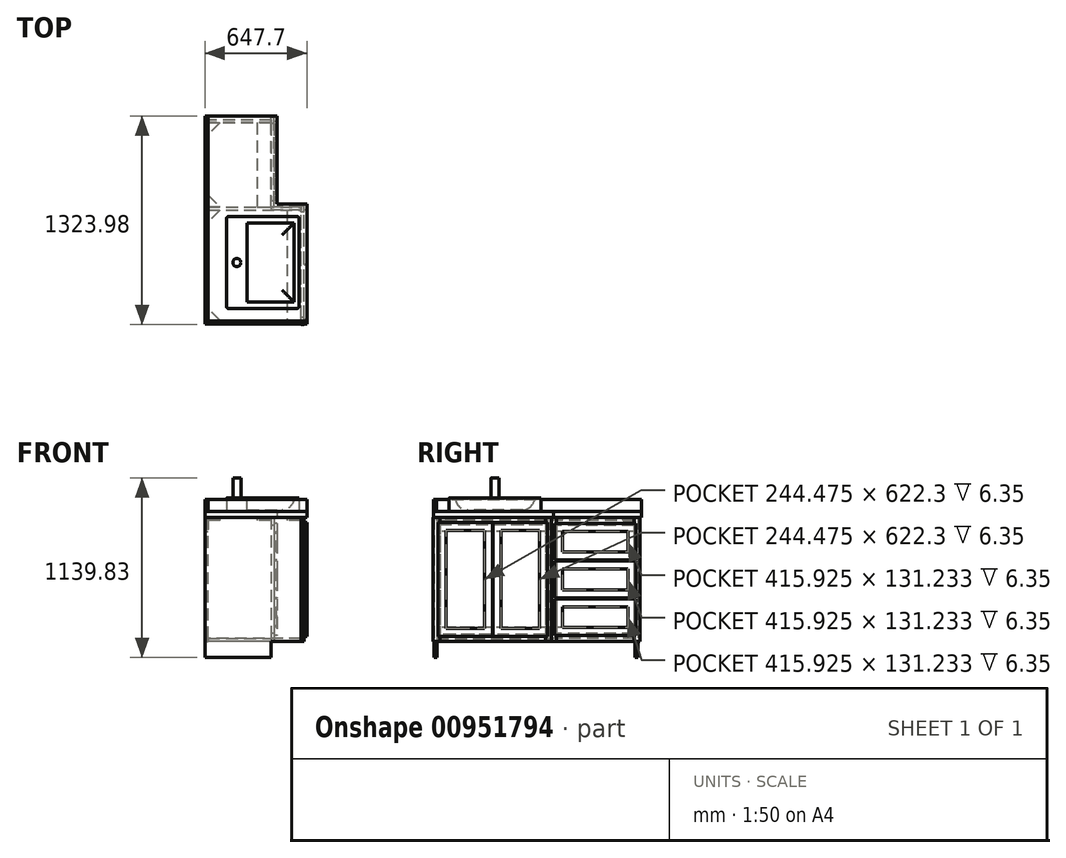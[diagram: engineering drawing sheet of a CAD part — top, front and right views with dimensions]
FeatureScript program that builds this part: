
annotation { "Feature Type Name" : "Feature", "Feature Type Description" : "" }
export const myFeature = defineFeature(function(context is Context, id is Id, definition is map)
    precondition{}
    {
        {
            var Q0;
            Q0=qCreatedBy(makeId("Top.planeOp"),FACE);
            var sketch = newSketch(context, id + "F0", { "sketchPlane" : qUnion([Q0])});
            skLineSegment(sketch, "E0", {"start": v(-384.18, 0) * mm, "end": v(384.18, 0) * mm});
            skLineSegment(sketch, "E1", {"start": v(-384.18, 0) * mm, "end": v(-1247.78, 0) * mm});
            skLineSegment(sketch, "E2", {"start": v(-1247.78, 0) * mm, "end": v(-1247.78, 2298.7) * mm});
            skLineSegment(sketch, "E3", {"start": v(-1247.78, 2298.7) * mm, "end": v(206.37, 2298.7) * mm});
            skLineSegment(sketch, "E4", {"start": v(206.37, 2298.7) * mm, "end": v(206.37, 1555.75) * mm});
            skLineSegment(sketch, "E5", {"start": v(206.37, 1555.75) * mm, "end": v(574.68, 1555.75) * mm});
            skLineSegment(sketch, "E6", {"start": v(574.68, 1555.75) * mm, "end": v(574.68, 0) * mm});
            skLineSegment(sketch, "E7", {"start": v(574.68, 0) * mm, "end": v(384.18, 0) * mm});
            skLineSegment(sketch, "E8", {"start": v(206.37, 1555.75) * mm, "end": v(-1247.78, 1555.75) * mm, "construction": true});
            skLineSegment(sketch, "E9", {"start": v(219.08, 1327.15) * mm, "end": v(219.08, 819.15) * mm, "construction": true});
            skLineSegment(sketch, "E10", {"start": v(-136.53, 1073.15) * mm, "end": v(574.68, 1073.15) * mm, "construction": true});
            skPoint(sketch, "E11", {"position": v(219.08, 1073.15) * mm});
            skLineSegment(sketch, "E12", {"start": v(-1247.78, 1320.8) * mm, "end": v(-790.58, 1320.8) * mm, "construction": true});
            skLineSegment(sketch, "E13", {"start": v(-790.57, 1320.8) * mm, "end": v(-790.57, 762) * mm, "construction": true});
            skLineSegment(sketch, "E14", {"start": v(-790.58, 762) * mm, "end": v(-600.07, 762) * mm, "construction": true});
            skLineSegment(sketch, "E15", {"start": v(-600.07, 762) * mm, "end": v(-600.07, 0) * mm, "construction": true});
            skEllipse(sketch, "E16", {"center": v(219.08, 1073.15) * mm, "majorRadius": 355.6 * mm, "minorRadius": 254 * mm, "majorAxis": v(1, 0)});
            skLineSegment(sketch, "E17", {"start": v(-1228.73, 1320.8) * mm, "end": v(-1228.72, 0) * mm, "construction": true});
            skLineSegment(sketch, "E18", {"start": v(-1228.72, 19.05) * mm, "end": v(-600.07, 19.05) * mm, "construction": true});
            skLineSegment(sketch, "E19.bottom", {"start": v(-650.87, 98.43) * mm, "end": v(-1111.25, 98.43) * mm});
            skLineSegment(sketch, "E19.top", {"start": v(-650.87, 682.63) * mm, "end": v(-1111.25, 682.63) * mm});
            skLineSegment(sketch, "E19.left", {"start": v(-650.87, 98.43) * mm, "end": v(-650.87, 682.63) * mm});
            skLineSegment(sketch, "E19.right", {"start": v(-1111.25, 98.43) * mm, "end": v(-1111.25, 682.63) * mm});
            skPoint(sketch, "E19.middle", {"position": v(-881.06, 390.53) * mm});
            skLineSegment(sketch, "E20", {"start": v(-1111.25, 390.53) * mm, "end": v(-1228.73, 390.53) * mm, "construction": true});
            skLineSegment(sketch, "E21", {"start": v(-881.06, 98.43) * mm, "end": v(-881.06, 19.05) * mm, "construction": true});
            skLineSegment(sketch, "E22", {"start": v(-650.87, 390.53) * mm, "end": v(-600.07, 390.53) * mm, "construction": true});
            skLineSegment(sketch, "E23", {"start": v(-650.87, 682.63) * mm, "end": v(-650.87, 762) * mm, "construction": true});
            skSolve(sketch);
        }
        {
            var Q0;
            Q0=qCreatedBy(makeId("Top.planeOp"),FACE);
            var sketch = newSketch(context, id + "F1", { "sketchPlane" : qUnion([Q0])});
            skLineSegment(sketch, "E24.bottom", {"start": v(-1247.78, 3.17) * mm, "end": v(-638.17, 3.17) * mm});
            skLineSegment(sketch, "E24.top", {"start": v(-1247.78, 22.23) * mm, "end": v(-638.17, 22.23) * mm});
            skLineSegment(sketch, "E24.left", {"start": v(-1247.78, 3.17) * mm, "end": v(-1247.78, 22.22) * mm});
            skLineSegment(sketch, "E24.right", {"start": v(-638.17, 3.17) * mm, "end": v(-638.17, 22.23) * mm});
            skLineSegment(sketch, "E25.bottom", {"start": v(-1247.78, 742.95) * mm, "end": v(-638.18, 742.95) * mm});
            skLineSegment(sketch, "E25.top", {"start": v(-1247.78, 723.9) * mm, "end": v(-638.18, 723.9) * mm});
            skLineSegment(sketch, "E25.left", {"start": v(-1247.78, 742.95) * mm, "end": v(-1247.78, 723.9) * mm});
            skLineSegment(sketch, "E25.right", {"start": v(-638.18, 742.95) * mm, "end": v(-638.18, 723.9) * mm});
            skLineSegment(sketch, "E26.bottom", {"start": v(-1247.78, 1298.58) * mm, "end": v(-828.67, 1298.58) * mm});
            skLineSegment(sketch, "E26.top", {"start": v(-1247.78, 1279.53) * mm, "end": v(-828.67, 1279.53) * mm});
            skLineSegment(sketch, "E26.left", {"start": v(-1247.78, 1298.58) * mm, "end": v(-1247.78, 1279.53) * mm});
            skLineSegment(sketch, "E26.right", {"start": v(-828.67, 1298.58) * mm, "end": v(-828.67, 1279.53) * mm});
            skLineSegment(sketch, "E27.bottom", {"start": v(-619.12, 0) * mm, "end": v(-638.17, 0) * mm, "construction": true});
            skLineSegment(sketch, "E27.top", {"start": v(-619.12, 50.8) * mm, "end": v(-638.17, 50.8) * mm, "construction": true});
            skLineSegment(sketch, "E27.left", {"start": v(-619.12, 0) * mm, "end": v(-619.12, 50.8) * mm, "construction": true});
            skLineSegment(sketch, "E27.right", {"start": v(-638.17, 0) * mm, "end": v(-638.17, 50.8) * mm, "construction": true});
            skLineSegment(sketch, "E28.bottom", {"start": v(-619.12, 692.15) * mm, "end": v(-638.18, 692.15) * mm, "construction": true});
            skLineSegment(sketch, "E28.top", {"start": v(-619.12, 742.95) * mm, "end": v(-638.18, 742.95) * mm, "construction": true});
            skLineSegment(sketch, "E28.left", {"start": v(-619.12, 692.15) * mm, "end": v(-619.12, 742.95) * mm, "construction": true});
            skLineSegment(sketch, "E28.right", {"start": v(-638.18, 692.15) * mm, "end": v(-638.18, 742.95) * mm, "construction": true});
            skLineSegment(sketch, "E29.bottom", {"start": v(-809.62, 1301.75) * mm, "end": v(-828.67, 1301.75) * mm, "construction": true});
            skLineSegment(sketch, "E29.top", {"start": v(-809.62, 1250.95) * mm, "end": v(-828.67, 1250.95) * mm, "construction": true});
            skLineSegment(sketch, "E29.left", {"start": v(-809.62, 1301.75) * mm, "end": v(-809.62, 1250.95) * mm, "construction": true});
            skLineSegment(sketch, "E29.right", {"start": v(-828.67, 1301.75) * mm, "end": v(-828.67, 1250.95) * mm, "construction": true});
            skLineSegment(sketch, "E30", {"start": v(-828.67, 1250.95) * mm, "end": v(-828.67, 793.75) * mm, "construction": true});
            skLineSegment(sketch, "E31", {"start": v(-809.62, 1250.95) * mm, "end": v(-809.62, 793.75) * mm, "construction": true});
            skLineSegment(sketch, "E32", {"start": v(-638.18, 692.15) * mm, "end": v(-638.17, 50.8) * mm, "construction": true});
            skLineSegment(sketch, "E33", {"start": v(-619.12, 50.8) * mm, "end": v(-619.12, 692.15) * mm, "construction": true});
            skLineSegment(sketch, "E34.bottom", {"start": v(-828.67, 793.75) * mm, "end": v(-809.62, 793.75) * mm, "construction": true});
            skLineSegment(sketch, "E34.top", {"start": v(-828.67, 742.95) * mm, "end": v(-809.62, 742.95) * mm, "construction": true});
            skLineSegment(sketch, "E34.left", {"start": v(-828.67, 793.75) * mm, "end": v(-828.67, 742.95) * mm, "construction": true});
            skLineSegment(sketch, "E34.right", {"start": v(-809.62, 793.75) * mm, "end": v(-809.62, 742.95) * mm, "construction": true});
            skSolve(sketch);
        }
        {
            var Q0;
            Q0 = qSketchRegion(id + "F1", true);
            extrude(context, id + "F2", {"entities" : qUnion([Q0]), "depth" : 889 * mm, "offsetDistance" : 25.4 * mm});
        }
        {
            var Q0;
            Q0=makeQuery(id+"F2.opExtrude","SWEPT_FACE",FACE,{"disambiguationData":[OSD([sQuery(id+"F1.wireOp",EDGE,"E24.bottom")])]});
            var sketch = newSketch(context, id + "F3", { "sketchPlane" : qUnion([Q0])});
            skLineSegment(sketch, "E35.bottom", {"start": v(-1247.78, 0) * mm, "end": v(-638.17, 0) * mm, "construction": true});
            skLineSegment(sketch, "E35.top", {"start": v(-1247.78, 101.6) * mm, "end": v(-638.17, 101.6) * mm, "construction": true});
            skLineSegment(sketch, "E35.left", {"start": v(-1247.78, 0) * mm, "end": v(-1247.78, 101.6) * mm, "construction": true});
            skLineSegment(sketch, "E35.right", {"start": v(-638.17, 0) * mm, "end": v(-638.17, 101.6) * mm});
            skLineSegment(sketch, "E36", {"start": v(-828.67, 101.6) * mm, "end": v(-828.67, 0) * mm});
            skLineSegment(sketch, "E37", {"start": v(-828.67, 101.6) * mm, "end": v(-638.17, 101.6) * mm});
            skLineSegment(sketch, "E38", {"start": v(-828.67, 0) * mm, "end": v(-638.17, 0) * mm});
            skSolve(sketch);
        }
        {
            var Q0;
            Q0 = qSketchRegion(id + "F3", true);
            extrude(context, id + "F4", {"entities" : qUnion([Q0]), "operationType" : NewBodyOperationType.REMOVE, "endBound" : BoundingType.THROUGH_ALL, "oppositeDirection" : true, "depth" : 25.4 * mm, "offsetDistance" : 25.4 * mm});
        }
        {
            var Q0;
            Q0=makeQuery(id+"F2.opExtrude","SWEPT_FACE",FACE,{"disambiguationData":[OSD([sQuery(id+"F1.wireOp",EDGE,"E24.right")])]});
            var sketch = newSketch(context, id + "F5", { "sketchPlane" : qUnion([Q0])});
            skLineSegment(sketch, "E39.bottom", {"start": v(-3.17, 889) * mm, "end": v(41.28, 889) * mm});
            skLineSegment(sketch, "E39.top", {"start": v(-3.17, 101.6) * mm, "end": v(41.28, 101.6) * mm});
            skLineSegment(sketch, "E39.left", {"start": v(-3.17, 889) * mm, "end": v(-3.17, 101.6) * mm});
            skLineSegment(sketch, "E39.right", {"start": v(41.28, 889) * mm, "end": v(41.28, 101.6) * mm});
            skLineSegment(sketch, "E40.bottom", {"start": v(711.2, 889) * mm, "end": v(749.3, 889) * mm});
            skLineSegment(sketch, "E40.top", {"start": v(711.2, 101.6) * mm, "end": v(749.3, 101.6) * mm});
            skLineSegment(sketch, "E40.left", {"start": v(711.2, 889) * mm, "end": v(711.2, 101.6) * mm});
            skLineSegment(sketch, "E40.right", {"start": v(749.3, 889) * mm, "end": v(749.3, 101.6) * mm});
            skSolve(sketch);
        }
        {
            var Q0;
            Q0 = qSketchRegion(id + "F5", true);
            extrude(context, id + "F6", {"entities" : qUnion([Q0]), "depth" : 19.05 * mm, "offsetDistance" : 25.4 * mm});
        }
        {
            var Q0;
            Q0=makeQuery(id+"F2.opExtrude","SWEPT_FACE",FACE,{"disambiguationData":[OSD([sQuery(id+"F1.wireOp",EDGE,"E26.right")])]});
            var sketch = newSketch(context, id + "F7", { "sketchPlane" : qUnion([Q0])});
            skLineSegment(sketch, "E41.bottom", {"start": v(1273.17, 889) * mm, "end": v(1311.27, 889) * mm});
            skLineSegment(sketch, "E41.top", {"start": v(1273.18, 101.6) * mm, "end": v(1311.27, 101.6) * mm});
            skLineSegment(sketch, "E41.left", {"start": v(1273.17, 889) * mm, "end": v(1273.17, 101.6) * mm});
            skLineSegment(sketch, "E41.right", {"start": v(1311.27, 889) * mm, "end": v(1311.27, 101.6) * mm});
            skLineSegment(sketch, "E42.bottom", {"start": v(742.95, 889) * mm, "end": v(781.05, 889) * mm});
            skLineSegment(sketch, "E42.top", {"start": v(742.95, 101.6) * mm, "end": v(781.05, 101.6) * mm});
            skLineSegment(sketch, "E42.left", {"start": v(742.95, 889) * mm, "end": v(742.95, 101.6) * mm});
            skLineSegment(sketch, "E42.right", {"start": v(781.05, 889) * mm, "end": v(781.05, 101.6) * mm});
            skSolve(sketch);
        }
        {
            var Q0;
            Q0 = qSketchRegion(id + "F7", true);
            extrude(context, id + "F8", {"entities" : qUnion([Q0]), "depth" : 19.05 * mm, "offsetDistance" : 25.4 * mm});
        }
        {
            var Q0;
            Q0=makeQuery(id+"F4.boolean.opBoolean","COPY",FACE,{"disambiguationData":[TD([makeQuery(id+"F2.opExtrude","SWEPT_FACE",FACE,{"disambiguationData":[OSD([sQuery(id+"F1.wireOp",EDGE,"E24.bottom")])]})])],"derivedFrom":makeQuery(id+"F4.opExtrude","SWEPT_FACE",FACE,{"disambiguationData":[OSD([sQuery(id+"F3.wireOp",EDGE,"E37")])]})});
            var sketch = newSketch(context, id + "F9", { "sketchPlane" : qUnion([Q0])});
            skLineSegment(sketch, "E43", {"start": v(-638.18, -22.22) * mm, "end": v(-1228.73, -22.23) * mm});
            skLineSegment(sketch, "E44", {"start": v(-638.18, -22.23) * mm, "end": v(-638.18, -723.9) * mm});
            skLineSegment(sketch, "E45", {"start": v(-828.67, -723.9) * mm, "end": v(-638.17, -723.9) * mm});
            skLineSegment(sketch, "E46", {"start": v(-828.67, -723.9) * mm, "end": v(-828.67, -1279.53) * mm});
            skLineSegment(sketch, "E47", {"start": v(-828.67, -1279.53) * mm, "end": v(-1228.73, -1279.53) * mm});
            skLineSegment(sketch, "E48", {"start": v(-1228.73, -1279.53) * mm, "end": v(-1228.73, -22.23) * mm});
            skSolve(sketch);
        }
        {
            var Q0;
            Q0 = qSketchRegion(id + "F9", true);
            extrude(context, id + "F10", {"entities" : qUnion([Q0]), "oppositeDirection" : true, "depth" : 19.05 * mm, "offsetDistance" : 25.4 * mm});
        }
        {
            var Q0;
            Q0=makeQuery(id+"F2.opExtrude","CAP_FACE",FACE,{"disambiguationData":[OSD([sQuery(id+"F1.wireOp",EDGE,"E25.bottom"),sQuery(id+"F1.wireOp",EDGE,"E25.top"),sQuery(id+"F1.wireOp",EDGE,"E25.left"),sQuery(id+"F1.wireOp",EDGE,"E25.right")])],"isStart":true});
            var sketch = newSketch(context, id + "F11", { "sketchPlane" : qUnion([Q0])});
            skLineSegment(sketch, "E49.0", {"start": v(-1247.78, -742.95) * mm, "end": v(-828.68, -742.95) * mm});
            skLineSegment(sketch, "E50.0", {"start": v(-828.67, -742.95) * mm, "end": v(-828.67, -723.9) * mm});
            skLineSegment(sketch, "E51.0", {"start": v(-1247.78, -723.9) * mm, "end": v(-828.67, -723.9) * mm});
            skLineSegment(sketch, "E52.0", {"start": v(-1247.78, -742.95) * mm, "end": v(-1247.78, -723.9) * mm});
            skSolve(sketch);
        }
        {
            var Q0;
            Q0 = qSketchRegion(id + "F11", true);
            extrude(context, id + "F12", {"entities" : qUnion([Q0]), "operationType" : NewBodyOperationType.REMOVE, "oppositeDirection" : true, "depth" : 120.65 * mm, "offsetDistance" : 25.4 * mm});
        }
        {
            var Q0;
            Q0=makeQuery(id+"F2.opExtrude","SWEPT_FACE",FACE,{"disambiguationData":[OSD([sQuery(id+"F1.wireOp",EDGE,"E25.bottom")])]});
            var sketch = newSketch(context, id + "F13", { "sketchPlane" : qUnion([Q0])});
            skLineSegment(sketch, "E53.bottom", {"start": v(1247.78, 120.65) * mm, "end": v(1228.73, 120.65) * mm});
            skLineSegment(sketch, "E53.top", {"start": v(1247.78, 889) * mm, "end": v(1228.73, 889) * mm});
            skLineSegment(sketch, "E53.left", {"start": v(1247.78, 120.65) * mm, "end": v(1247.78, 889) * mm});
            skLineSegment(sketch, "E53.right", {"start": v(1228.73, 120.65) * mm, "end": v(1228.73, 889) * mm});
            skSolve(sketch);
        }
        {
            var Q0;
            Q0 = qSketchRegion(id + "F13", true);
            extrude(context, id + "F14", {"entities" : qUnion([Q0]), "operationType" : NewBodyOperationType.REMOVE, "endBound" : BoundingType.UP_TO_NEXT, "oppositeDirection" : true, "depth" : 25.4 * mm, "offsetDistance" : 25.4 * mm});
        }
        {
            var Q0;
            Q0=makeQuery(id+"F6.opExtrude","CAP_FACE",FACE,{"disambiguationData":[OSD([sQuery(id+"F5.wireOp",EDGE,"E39.bottom"),sQuery(id+"F5.wireOp",EDGE,"E39.top"),sQuery(id+"F5.wireOp",EDGE,"E39.left"),sQuery(id+"F5.wireOp",EDGE,"E39.right")])],"isStart":false});
            var sketch = newSketch(context, id + "F15", { "sketchPlane" : qUnion([Q0])});
            skLineSegment(sketch, "E54.bottom", {"start": v(41.28, 889) * mm, "end": v(711.2, 889) * mm});
            skLineSegment(sketch, "E54.top", {"start": v(41.28, 844.55) * mm, "end": v(711.2, 844.55) * mm});
            skLineSegment(sketch, "E54.left", {"start": v(41.28, 889) * mm, "end": v(41.28, 844.55) * mm});
            skLineSegment(sketch, "E54.right", {"start": v(711.2, 889) * mm, "end": v(711.2, 844.55) * mm});
            skLineSegment(sketch, "E55.bottom", {"start": v(711.2, 101.6) * mm, "end": v(41.28, 101.6) * mm});
            skLineSegment(sketch, "E55.top", {"start": v(711.2, 146.05) * mm, "end": v(41.28, 146.05) * mm});
            skLineSegment(sketch, "E55.left", {"start": v(711.2, 101.6) * mm, "end": v(711.2, 146.05) * mm});
            skLineSegment(sketch, "E55.right", {"start": v(41.28, 101.6) * mm, "end": v(41.28, 146.05) * mm});
            skSolve(sketch);
        }
        {
            var Q0;
            Q0 = qSketchRegion(id + "F15", true);
            extrude(context, id + "F16", {"entities" : qUnion([Q0]), "oppositeDirection" : true, "depth" : 19.05 * mm, "offsetDistance" : 25.4 * mm});
        }
        {
            var Q0;
            Q0=makeQuery(id+"F8.opExtrude","SWEPT_FACE",FACE,{"disambiguationData":[OSD([sQuery(id+"F7.wireOp",EDGE,"E42.right")])]});
            var sketch = newSketch(context, id + "F17", { "sketchPlane" : qUnion([Q0])});
            skLineSegment(sketch, "E56.bottom", {"start": v(809.62, 889) * mm, "end": v(828.67, 889) * mm});
            skLineSegment(sketch, "E56.top", {"start": v(809.62, 838.2) * mm, "end": v(828.67, 838.2) * mm});
            skLineSegment(sketch, "E56.left", {"start": v(809.62, 889) * mm, "end": v(809.62, 838.2) * mm});
            skLineSegment(sketch, "E56.right", {"start": v(828.67, 889) * mm, "end": v(828.67, 838.2) * mm});
            skLineSegment(sketch, "E57.bottom", {"start": v(809.62, 101.6) * mm, "end": v(828.67, 101.6) * mm});
            skLineSegment(sketch, "E57.top", {"start": v(809.62, 152.4) * mm, "end": v(828.67, 152.4) * mm});
            skLineSegment(sketch, "E57.left", {"start": v(809.62, 101.6) * mm, "end": v(809.62, 152.4) * mm});
            skLineSegment(sketch, "E57.right", {"start": v(828.67, 101.6) * mm, "end": v(828.67, 152.4) * mm});
            skSolve(sketch);
        }
        {
            var Q0;
            Q0 = qSketchRegion(id + "F17", true);
            var Q1;
            Q1=makeQuery(id+"F8.opExtrude","SWEPT_FACE",FACE,{"disambiguationData":[OSD([sQuery(id+"F7.wireOp",EDGE,"E41.left")])]});
            extrude(context, id + "F18", {"entities" : qUnion([Q0]), "endBound" : BoundingType.UP_TO_SURFACE, "depth" : 25.4 * mm, "endBoundEntityFace" : qUnion([Q1]), "offsetDistance" : 25.4 * mm});
        }
        {
            var Q0;
            Q0=makeQuery(id+"F2.opExtrude","SWEPT_FACE",FACE,{"disambiguationData":[OSD([sQuery(id+"F1.wireOp",EDGE,"E24.top")])]});
            var sketch = newSketch(context, id + "F19", { "sketchPlane" : qUnion([Q0])});
            skLineSegment(sketch, "E58.bottom", {"start": v(1247.78, 889) * mm, "end": v(1228.72, 889) * mm});
            skLineSegment(sketch, "E58.top", {"start": v(1247.78, 800.1) * mm, "end": v(1228.72, 800.1) * mm});
            skLineSegment(sketch, "E58.left", {"start": v(1247.78, 889) * mm, "end": v(1247.78, 800.1) * mm});
            skLineSegment(sketch, "E58.right", {"start": v(1228.72, 889) * mm, "end": v(1228.72, 800.1) * mm});
            skLineSegment(sketch, "E59.bottom", {"start": v(1247.78, 101.6) * mm, "end": v(1228.73, 101.6) * mm});
            skLineSegment(sketch, "E59.top", {"start": v(1247.78, 190.5) * mm, "end": v(1228.73, 190.5) * mm});
            skLineSegment(sketch, "E59.left", {"start": v(1247.78, 101.6) * mm, "end": v(1247.78, 190.5) * mm});
            skLineSegment(sketch, "E59.right", {"start": v(1228.73, 101.6) * mm, "end": v(1228.73, 190.5) * mm});
            skSolve(sketch);
        }
        {
            var Q0;
            Q0 = qSketchRegion(id + "F19", true);
            var Q1;
            Q1=makeQuery(id+"F2.opExtrude","SWEPT_FACE",FACE,{"disambiguationData":[OSD([sQuery(id+"F1.wireOp",EDGE,"E26.top")])]});
            extrude(context, id + "F20", {"entities" : qUnion([Q0]), "endBound" : BoundingType.UP_TO_SURFACE, "depth" : 25.4 * mm, "endBoundEntityFace" : qUnion([Q1]), "offsetDistance" : 25.4 * mm});
        }
        {
            var Q0;
            Q0=makeQuery(id+"F2.opExtrude","SWEPT_FACE",FACE,{"disambiguationData":[OSD([sQuery(id+"F1.wireOp",EDGE,"E24.top")])]});
            var sketch = newSketch(context, id + "F21", { "sketchPlane" : qUnion([Q0])});
            skLineSegment(sketch, "E60.bottom", {"start": v(638.17, 889) * mm, "end": v(727.07, 889) * mm});
            skLineSegment(sketch, "E60.top", {"start": v(638.17, 869.95) * mm, "end": v(727.07, 869.95) * mm});
            skLineSegment(sketch, "E60.left", {"start": v(638.17, 889) * mm, "end": v(638.17, 869.95) * mm});
            skLineSegment(sketch, "E60.right", {"start": v(727.07, 889) * mm, "end": v(727.07, 869.95) * mm});
            skSolve(sketch);
        }
        {
            var Q0;
            Q0 = qSketchRegion(id + "F21", true);
            var Q1;
            Q1=makeQuery(id+"F2.opExtrude","SWEPT_FACE",FACE,{"disambiguationData":[OSD([sQuery(id+"F1.wireOp",EDGE,"E25.top")])]});
            extrude(context, id + "F22", {"entities" : qUnion([Q0]), "endBound" : BoundingType.UP_TO_SURFACE, "depth" : 25.4 * mm, "endBoundEntityFace" : qUnion([Q1]), "offsetDistance" : 25.4 * mm});
        }
        {
            var Q0;
            Q0=makeQuery(id+"F2.opExtrude","SWEPT_FACE",FACE,{"disambiguationData":[OSD([sQuery(id+"F1.wireOp",EDGE,"E25.bottom")])]});
            var sketch = newSketch(context, id + "F23", { "sketchPlane" : qUnion([Q0])});
            skLineSegment(sketch, "E61.bottom", {"start": v(828.67, 889) * mm, "end": v(917.57, 889) * mm});
            skLineSegment(sketch, "E61.top", {"start": v(828.67, 869.95) * mm, "end": v(917.57, 869.95) * mm});
            skLineSegment(sketch, "E61.left", {"start": v(828.67, 889) * mm, "end": v(828.67, 869.95) * mm});
            skLineSegment(sketch, "E61.right", {"start": v(917.57, 889) * mm, "end": v(917.57, 869.95) * mm});
            skSolve(sketch);
        }
        {
            var Q0;
            Q0 = qSketchRegion(id + "F23", true);
            var Q1;
            Q1=makeQuery(id+"F2.opExtrude","SWEPT_FACE",FACE,{"disambiguationData":[OSD([sQuery(id+"F1.wireOp",EDGE,"E26.top")])]});
            extrude(context, id + "F24", {"entities" : qUnion([Q0]), "endBound" : BoundingType.UP_TO_SURFACE, "depth" : 25.4 * mm, "endBoundEntityFace" : qUnion([Q1]), "offsetDistance" : 25.4 * mm});
        }
        {
            var Q0;
            Q0=makeQuery(id+"F2.opExtrude","CAP_FACE",FACE,{"disambiguationData":[OSD([sQuery(id+"F1.wireOp",EDGE,"E24.bottom"),sQuery(id+"F1.wireOp",EDGE,"E24.top"),sQuery(id+"F1.wireOp",EDGE,"E24.left"),sQuery(id+"F1.wireOp",EDGE,"E24.right")])],"isStart":false});
            var sketch = newSketch(context, id + "F25", { "sketchPlane" : qUnion([Q0])});
            skLineSegment(sketch, "E62", {"start": v(-1152.52, 22.23) * mm, "end": v(-1228.72, 98.43) * mm});
            skLineSegment(sketch, "E63", {"start": v(-1228.72, 98.43) * mm, "end": v(-1228.72, 22.23) * mm});
            skLineSegment(sketch, "E64", {"start": v(-1228.72, 22.23) * mm, "end": v(-1152.52, 22.23) * mm});
            skLineSegment(sketch, "E65", {"start": v(-1228.72, 647.7) * mm, "end": v(-1228.72, 723.9) * mm});
            skLineSegment(sketch, "E66", {"start": v(-1228.73, 723.9) * mm, "end": v(-1152.53, 723.9) * mm});
            skLineSegment(sketch, "E67", {"start": v(-1152.53, 723.9) * mm, "end": v(-1228.73, 647.7) * mm});
            skLineSegment(sketch, "E68", {"start": v(-1152.53, 742.95) * mm, "end": v(-1228.73, 742.95) * mm});
            skLineSegment(sketch, "E69", {"start": v(-1228.73, 742.95) * mm, "end": v(-1228.73, 819.15) * mm});
            skLineSegment(sketch, "E70", {"start": v(-1228.72, 819.15) * mm, "end": v(-1152.52, 742.95) * mm});
            skLineSegment(sketch, "E71", {"start": v(-1228.72, 1203.33) * mm, "end": v(-1228.72, 1279.53) * mm});
            skLineSegment(sketch, "E72", {"start": v(-1228.72, 1279.53) * mm, "end": v(-1152.52, 1279.53) * mm});
            skLineSegment(sketch, "E73", {"start": v(-1152.52, 1279.53) * mm, "end": v(-1228.72, 1203.33) * mm});
            skSolve(sketch);
        }
        {
            var Q0;
            Q0 = qSketchRegion(id + "F25", true);
            extrude(context, id + "F26", {"entities" : qUnion([Q0]), "oppositeDirection" : true, "depth" : 19.05 * mm, "offsetDistance" : 25.4 * mm});
        }
        {
            var Q0;
            Q0=makeQuery(id+"F6.opExtrude","CAP_FACE",FACE,{"disambiguationData":[OSD([sQuery(id+"F5.wireOp",EDGE,"E39.bottom"),sQuery(id+"F5.wireOp",EDGE,"E39.top"),sQuery(id+"F5.wireOp",EDGE,"E39.left"),sQuery(id+"F5.wireOp",EDGE,"E39.right")])],"isStart":false});
            var sketch = newSketch(context, id + "F27", { "sketchPlane" : qUnion([Q0])});
            skLineSegment(sketch, "E74.bottom", {"start": v(28.58, 857.25) * mm, "end": v(374.65, 857.25) * mm});
            skLineSegment(sketch, "E74.top", {"start": v(28.58, 133.35) * mm, "end": v(374.65, 133.35) * mm});
            skLineSegment(sketch, "E74.left", {"start": v(28.58, 857.25) * mm, "end": v(28.58, 133.35) * mm});
            skLineSegment(sketch, "E74.right", {"start": v(374.65, 857.25) * mm, "end": v(374.65, 133.35) * mm});
            skLineSegment(sketch, "E75.bottom", {"start": v(377.83, 133.35) * mm, "end": v(723.9, 133.35) * mm});
            skLineSegment(sketch, "E75.top", {"start": v(377.83, 857.25) * mm, "end": v(723.9, 857.25) * mm});
            skLineSegment(sketch, "E75.left", {"start": v(377.83, 133.35) * mm, "end": v(377.83, 857.25) * mm});
            skLineSegment(sketch, "E75.right", {"start": v(723.9, 133.35) * mm, "end": v(723.9, 857.25) * mm});
            skSolve(sketch);
        }
        {
            var Q0;
            Q0 = qSketchRegion(id + "F27", true);
            extrude(context, id + "F28", {"entities" : qUnion([Q0]), "depth" : 19.05 * mm, "offsetDistance" : 25.4 * mm});
        }
        {
            var Q0;
            Q0=makeQuery(id+"F28.opExtrude","CAP_FACE",FACE,{"disambiguationData":[OSD([sQuery(id+"F27.wireOp",EDGE,"E74.bottom"),sQuery(id+"F27.wireOp",EDGE,"E74.top"),sQuery(id+"F27.wireOp",EDGE,"E74.left"),sQuery(id+"F27.wireOp",EDGE,"E74.right")])],"isStart":false});
            var sketch = newSketch(context, id + "F29", { "sketchPlane" : qUnion([Q0])});
            skLineSegment(sketch, "E76.0", {"start": v(323.85, 806.45) * mm, "end": v(79.38, 806.45) * mm});
            skLineSegment(sketch, "E76.1", {"start": v(323.85, 184.15) * mm, "end": v(323.85, 806.45) * mm});
            skLineSegment(sketch, "E76.2", {"start": v(79.38, 184.15) * mm, "end": v(323.85, 184.15) * mm});
            skLineSegment(sketch, "E76.3", {"start": v(79.38, 806.45) * mm, "end": v(79.38, 184.15) * mm});
            skLineSegment(sketch, "E77.0", {"start": v(673.1, 806.45) * mm, "end": v(428.63, 806.45) * mm});
            skLineSegment(sketch, "E77.1", {"start": v(673.1, 184.15) * mm, "end": v(673.1, 806.45) * mm});
            skLineSegment(sketch, "E77.2", {"start": v(428.63, 184.15) * mm, "end": v(673.1, 184.15) * mm});
            skLineSegment(sketch, "E77.3", {"start": v(428.63, 806.45) * mm, "end": v(428.63, 184.15) * mm});
            skSolve(sketch);
        }
        {
            var Q0;
            Q0 = qSketchRegion(id + "F29", true);
            extrude(context, id + "F30", {"entities" : qUnion([Q0]), "operationType" : NewBodyOperationType.REMOVE, "oppositeDirection" : true, "depth" : 6.35 * mm, "offsetDistance" : 25.4 * mm});
        }
        {
            var Q0;
            Q0=makeQuery(id+"F8.opExtrude","CAP_FACE",FACE,{"disambiguationData":[OSD([sQuery(id+"F7.wireOp",EDGE,"E41.bottom"),sQuery(id+"F7.wireOp",EDGE,"E41.top"),sQuery(id+"F7.wireOp",EDGE,"E41.left"),sQuery(id+"F7.wireOp",EDGE,"E41.right")])],"isStart":false});
            var sketch = newSketch(context, id + "F31", { "sketchPlane" : qUnion([Q0])});
            skLineSegment(sketch, "E78.bottom", {"start": v(768.35, 850.9) * mm, "end": v(1285.87, 850.9) * mm});
            skLineSegment(sketch, "E78.top", {"start": v(768.35, 618.07) * mm, "end": v(1285.87, 618.07) * mm});
            skLineSegment(sketch, "E78.left", {"start": v(768.35, 850.9) * mm, "end": v(768.35, 618.07) * mm});
            skLineSegment(sketch, "E78.right", {"start": v(1285.88, 850.9) * mm, "end": v(1285.88, 618.07) * mm});
            skLineSegment(sketch, "E79.bottom", {"start": v(1285.87, 611.72) * mm, "end": v(768.35, 611.72) * mm});
            skLineSegment(sketch, "E79.top", {"start": v(1285.87, 378.88) * mm, "end": v(768.35, 378.88) * mm});
            skLineSegment(sketch, "E79.left", {"start": v(1285.87, 611.72) * mm, "end": v(1285.87, 378.88) * mm});
            skLineSegment(sketch, "E79.right", {"start": v(768.35, 611.72) * mm, "end": v(768.35, 378.88) * mm});
            skLineSegment(sketch, "E80.bottom", {"start": v(768.35, 372.53) * mm, "end": v(1285.87, 372.53) * mm});
            skLineSegment(sketch, "E80.top", {"start": v(768.35, 139.7) * mm, "end": v(1285.87, 139.7) * mm});
            skLineSegment(sketch, "E80.left", {"start": v(768.35, 372.53) * mm, "end": v(768.35, 139.7) * mm});
            skLineSegment(sketch, "E80.right", {"start": v(1285.87, 372.53) * mm, "end": v(1285.87, 139.7) * mm});
            skSolve(sketch);
        }
        {
            var Q0;
            Q0 = qSketchRegion(id + "F31", true);
            extrude(context, id + "F32", {"entities" : qUnion([Q0]), "depth" : 19.05 * mm, "offsetDistance" : 25.4 * mm});
        }
        {
            var Q0;
            Q0=makeQuery(id+"F32.opExtrude","CAP_FACE",FACE,{"disambiguationData":[OSD([sQuery(id+"F31.wireOp",EDGE,"E78.bottom"),sQuery(id+"F31.wireOp",EDGE,"E78.top"),sQuery(id+"F31.wireOp",EDGE,"E78.left"),sQuery(id+"F31.wireOp",EDGE,"E78.right")])],"isStart":false});
            var sketch = newSketch(context, id + "F33", { "sketchPlane" : qUnion([Q0])});
            skLineSegment(sketch, "E81.0", {"start": v(1235.08, 668.87) * mm, "end": v(1235.08, 800.1) * mm});
            skLineSegment(sketch, "E81.1", {"start": v(819.15, 668.87) * mm, "end": v(1235.08, 668.87) * mm});
            skLineSegment(sketch, "E81.2", {"start": v(819.15, 800.1) * mm, "end": v(819.15, 668.87) * mm});
            skLineSegment(sketch, "E81.3", {"start": v(1235.08, 800.1) * mm, "end": v(819.15, 800.1) * mm});
            skLineSegment(sketch, "E82.0", {"start": v(819.15, 429.68) * mm, "end": v(1235.07, 429.68) * mm});
            skLineSegment(sketch, "E82.1", {"start": v(819.15, 560.92) * mm, "end": v(819.15, 429.68) * mm});
            skLineSegment(sketch, "E82.2", {"start": v(1235.07, 560.92) * mm, "end": v(819.15, 560.92) * mm});
            skLineSegment(sketch, "E82.3", {"start": v(1235.07, 429.68) * mm, "end": v(1235.07, 560.92) * mm});
            skLineSegment(sketch, "E83.0", {"start": v(819.15, 321.73) * mm, "end": v(819.15, 190.5) * mm});
            skLineSegment(sketch, "E83.1", {"start": v(1235.07, 321.73) * mm, "end": v(819.15, 321.73) * mm});
            skLineSegment(sketch, "E83.2", {"start": v(1235.07, 190.5) * mm, "end": v(1235.07, 321.73) * mm});
            skLineSegment(sketch, "E83.3", {"start": v(819.15, 190.5) * mm, "end": v(1235.07, 190.5) * mm});
            skSolve(sketch);
        }
        {
            var Q0;
            Q0 = qSketchRegion(id + "F33", true);
            extrude(context, id + "F34", {"entities" : qUnion([Q0]), "operationType" : NewBodyOperationType.REMOVE, "oppositeDirection" : true, "depth" : 6.35 * mm, "offsetDistance" : 25.4 * mm});
        }
        {
            var Q0;
            Q0=makeQuery(id+"F2.opExtrude","CAP_FACE",FACE,{"disambiguationData":[OSD([sQuery(id+"F1.wireOp",EDGE,"E24.bottom"),sQuery(id+"F1.wireOp",EDGE,"E24.top"),sQuery(id+"F1.wireOp",EDGE,"E24.left"),sQuery(id+"F1.wireOp",EDGE,"E24.right")])],"isStart":false});
            var sketch = newSketch(context, id + "F35", { "sketchPlane" : qUnion([Q0])});
            skLineSegment(sketch, "E84.0", {"start": v(-1247.78, 1320.8) * mm, "end": v(-790.58, 1320.8) * mm});
            skLineSegment(sketch, "E84.1", {"start": v(-790.57, 1320.8) * mm, "end": v(-790.57, 762) * mm});
            skLineSegment(sketch, "E84.2", {"start": v(-790.58, 762) * mm, "end": v(-600.07, 762) * mm});
            skLineSegment(sketch, "E84.3", {"start": v(-600.07, 762) * mm, "end": v(-600.07, 0) * mm});
            skLineSegment(sketch, "E84.4", {"start": v(-600.07, 0) * mm, "end": v(-1247.78, 0) * mm});
            skLineSegment(sketch, "E84.5", {"start": v(-1247.78, 0) * mm, "end": v(-1247.78, 1320.8) * mm});
            skPoint(sketch, "E85.orphan", {"position": v(-384.18, 0) * mm});
            skPoint(sketch, "E86.orphan", {"position": v(-1247.78, 2298.7) * mm});
            skSolve(sketch);
        }
        {
            var Q0;
            Q0 = qSketchRegion(id + "F35", true);
            extrude(context, id + "F36", {"entities" : qUnion([Q0]), "depth" : 38.1 * mm, "offsetDistance" : 25.4 * mm});
        }
        {
            var Q0;
            Q0=makeQuery(id+"F36.opExtrude","CAP_FACE",FACE,{"disambiguationData":[OSD([sQuery(id+"F35.wireOp",EDGE,"E84.0"),sQuery(id+"F35.wireOp",EDGE,"E84.1"),sQuery(id+"F35.wireOp",EDGE,"E84.2"),sQuery(id+"F35.wireOp",EDGE,"E84.3"),sQuery(id+"F35.wireOp",EDGE,"E84.4"),sQuery(id+"F35.wireOp",EDGE,"E84.5")])],"isStart":false});
            var sketch = newSketch(context, id + "F37", { "sketchPlane" : qUnion([Q0])});
            skLineSegment(sketch, "E87.0", {"start": v(-1228.73, 1320.8) * mm, "end": v(-1228.72, 0) * mm});
            skLineSegment(sketch, "E87.1", {"start": v(-1228.72, 0) * mm, "end": v(-1247.78, 0) * mm});
            skLineSegment(sketch, "E87.2", {"start": v(-1247.78, 0) * mm, "end": v(-1247.78, 1320.8) * mm});
            skLineSegment(sketch, "E87.3", {"start": v(-1247.78, 1320.8) * mm, "end": v(-1228.73, 1320.8) * mm});
            skPoint(sketch, "E88.orphan", {"position": v(-1247.78, 2298.7) * mm});
            skPoint(sketch, "E89.orphan", {"position": v(-790.58, 1320.8) * mm});
            skPoint(sketch, "E90.orphan", {"position": v(-384.18, 0) * mm});
            skSolve(sketch);
        }
        {
            var Q0;
            Q0 = qSketchRegion(id + "F37", true);
            extrude(context, id + "F38", {"entities" : qUnion([Q0]), "depth" : 76.2 * mm, "offsetDistance" : 25.4 * mm});
        }
        {
            var Q0;
            Q0=makeQuery(id+"F36.opExtrude","CAP_FACE",FACE,{"disambiguationData":[OSD([sQuery(id+"F35.wireOp",EDGE,"E84.0"),sQuery(id+"F35.wireOp",EDGE,"E84.1"),sQuery(id+"F35.wireOp",EDGE,"E84.2"),sQuery(id+"F35.wireOp",EDGE,"E84.3"),sQuery(id+"F35.wireOp",EDGE,"E84.4"),sQuery(id+"F35.wireOp",EDGE,"E84.5")])],"isStart":false});
            var sketch = newSketch(context, id + "F39", { "sketchPlane" : qUnion([Q0])});
            skLineSegment(sketch, "E91.0", {"start": v(-1228.72, 19.05) * mm, "end": v(-600.07, 19.05) * mm});
            skLineSegment(sketch, "E91.1", {"start": v(-600.07, 0) * mm, "end": v(-1228.72, 0) * mm});
            skLineSegment(sketch, "E91.2", {"start": v(-1228.72, 19.05) * mm, "end": v(-1228.72, 0) * mm});
            skLineSegment(sketch, "E91.3", {"start": v(-600.07, 19.05) * mm, "end": v(-600.07, 0) * mm});
            skPoint(sketch, "E92.orphan", {"position": v(-600.07, 762) * mm});
            skPoint(sketch, "E93.orphan", {"position": v(-384.18, 0) * mm});
            skPoint(sketch, "E94.orphan", {"position": v(-1228.73, 1320.8) * mm});
            skPoint(sketch, "E95.orphan", {"position": v(-1247.78, 0) * mm});
            skSolve(sketch);
        }
        {
            var Q0;
            Q0 = qSketchRegion(id + "F39", true);
            extrude(context, id + "F40", {"entities" : qUnion([Q0]), "depth" : 76.2 * mm, "offsetDistance" : 25.4 * mm});
        }
        {
            var Q0;
            Q0=makeQuery(id+"F36.opExtrude","CAP_FACE",FACE,{"disambiguationData":[OSD([sQuery(id+"F35.wireOp",EDGE,"E84.0"),sQuery(id+"F35.wireOp",EDGE,"E84.1"),sQuery(id+"F35.wireOp",EDGE,"E84.2"),sQuery(id+"F35.wireOp",EDGE,"E84.3"),sQuery(id+"F35.wireOp",EDGE,"E84.4"),sQuery(id+"F35.wireOp",EDGE,"E84.5")])],"isStart":false});
            var sketch = newSketch(context, id + "F41", { "sketchPlane" : qUnion([Q0])});
            skLineSegment(sketch, "E96.0", {"start": v(-663.57, 682.63) * mm, "end": v(-1098.55, 682.63) * mm});
            skLineSegment(sketch, "E96.1", {"start": v(-650.87, 111.13) * mm, "end": v(-650.87, 669.93) * mm});
            skLineSegment(sketch, "E96.2", {"start": v(-663.57, 98.43) * mm, "end": v(-1098.55, 98.43) * mm});
            skLineSegment(sketch, "E96.3", {"start": v(-1111.25, 111.13) * mm, "end": v(-1111.25, 669.93) * mm});
            skPoint(sketch, "E97.visualSharp", {"position": v(-1111.25, 682.63) * mm});
            skArc(sketch, "E97.filletArc", {"start": v(-1098.55, 682.63) * mm, "mid": v(-1107.53, 678.9) * mm, "end": v(-1111.25, 669.93) * mm});
            skPoint(sketch, "E98.visualSharp", {"position": v(-650.87, 682.63) * mm});
            skArc(sketch, "E98.filletArc", {"start": v(-650.87, 669.93) * mm, "mid": v(-654.6, 678.9) * mm, "end": v(-663.57, 682.63) * mm});
            skPoint(sketch, "E99.visualSharp", {"position": v(-650.87, 98.43) * mm});
            skArc(sketch, "E99.filletArc", {"start": v(-663.57, 98.43) * mm, "mid": v(-654.6, 102.14) * mm, "end": v(-650.87, 111.13) * mm});
            skPoint(sketch, "E100.visualSharp", {"position": v(-1111.25, 98.43) * mm});
            skArc(sketch, "E100.filletArc", {"start": v(-1111.25, 111.13) * mm, "mid": v(-1107.53, 102.14) * mm, "end": v(-1098.55, 98.43) * mm});
            skSolve(sketch);
        }
        {
            var Q0;
            Q0 = qSketchRegion(id + "F41", true);
            extrude(context, id + "F42", {"entities" : qUnion([Q0]), "depth" : 85.72 * mm, "offsetDistance" : 25.4 * mm});
        }
        {
            var Q0;
            Q0=makeQuery(id+"F42.opExtrude","CAP_FACE",FACE,{"disambiguationData":[OSD([sQuery(id+"F41.wireOp",EDGE,"E96.0"),sQuery(id+"F41.wireOp",EDGE,"E96.1"),sQuery(id+"F41.wireOp",EDGE,"E96.2"),sQuery(id+"F41.wireOp",EDGE,"E96.3"),sQuery(id+"F41.wireOp",EDGE,"E97.filletArc"),sQuery(id+"F41.wireOp",EDGE,"E98.filletArc"),sQuery(id+"F41.wireOp",EDGE,"E99.filletArc"),sQuery(id+"F41.wireOp",EDGE,"E100.filletArc")])],"isStart":false});
            var sketch = newSketch(context, id + "F43", { "sketchPlane" : qUnion([Q0])});
            skLineSegment(sketch, "E101.bottom", {"start": v(-979.54, 640.56) * mm, "end": v(-683.25, 640.56) * mm});
            skLineSegment(sketch, "E101.top", {"start": v(-979.54, 140.49) * mm, "end": v(-683.25, 140.49) * mm});
            skLineSegment(sketch, "E101.left", {"start": v(-979.54, 640.56) * mm, "end": v(-979.54, 140.49) * mm});
            skLineSegment(sketch, "E101.right", {"start": v(-683.25, 640.56) * mm, "end": v(-683.25, 140.49) * mm});
            skLineSegment(sketch, "E102", {"start": v(-650.87, 390.53) * mm, "end": v(-683.25, 390.53) * mm, "construction": true});
            skPoint(sketch, "E102.endSnap0", {"position": v(-683.25, 390.53) * mm});
            skSolve(sketch);
        }
        {
            var Q0;
            Q0 = qSketchRegion(id + "F43", true);
            extrude(context, id + "F44", {"entities" : qUnion([Q0]), "operationType" : NewBodyOperationType.REMOVE, "oppositeDirection" : true, "depth" : 76.2 * mm, "offsetDistance" : 25.4 * mm});
        }
        {
            var Q0;
            Q0=makeQuery(id+"F44.boolean.opBoolean","COPY",EDGE,{"derivedFrom":makeQuery(id+"F44.opExtrude","CAP_EDGE",EDGE,{"disambiguationData":[OSD([sQuery(id+"F43.wireOp",EDGE,"E101.bottom")])],"isStart":false})});
            var Q1;
            Q1=makeQuery(id+"F44.boolean.opBoolean","COPY",EDGE,{"derivedFrom":makeQuery(id+"F44.opExtrude","CAP_EDGE",EDGE,{"disambiguationData":[OSD([sQuery(id+"F43.wireOp",EDGE,"E101.top")])],"isStart":false})});
            var Q2;
            Q2=makeQuery(id+"F44.boolean.opBoolean","COPY",EDGE,{"derivedFrom":makeQuery(id+"F44.opExtrude","CAP_EDGE",EDGE,{"disambiguationData":[OSD([sQuery(id+"F43.wireOp",EDGE,"E101.right")])],"isStart":false})});
            fillet(context, id + "F45", {"entities" : qUnion([Q0, Q1, Q2]), "radius" : 76.2 * mm, "tangentPropagation" : true, "allowEdgeOverflow" : false});
        }
        {
            var Q0;
            Q0=makeQuery(id+"F42.opExtrude","CAP_FACE",FACE,{"disambiguationData":[OSD([sQuery(id+"F41.wireOp",EDGE,"E96.0"),sQuery(id+"F41.wireOp",EDGE,"E96.1"),sQuery(id+"F41.wireOp",EDGE,"E96.2"),sQuery(id+"F41.wireOp",EDGE,"E96.3"),sQuery(id+"F41.wireOp",EDGE,"E97.filletArc"),sQuery(id+"F41.wireOp",EDGE,"E98.filletArc"),sQuery(id+"F41.wireOp",EDGE,"E99.filletArc"),sQuery(id+"F41.wireOp",EDGE,"E100.filletArc")])],"isStart":false});
            var sketch = newSketch(context, id + "F46", { "sketchPlane" : qUnion([Q0])});
            skPoint(sketch, "E103.endSnap0", {"position": v(-979.54, 390.53) * mm});
            skCircle(sketch, "E104", {"center": v(-1045.4, 390.53) * mm, "radius": 25.3 * mm});
            skLineSegment(sketch, "E105", {"start": v(-979.54, 390.53) * mm, "end": v(-1111.25, 390.53) * mm, "construction": true});
            skSolve(sketch);
        }
        {
            var Q0;
            Q0 = qSketchRegion(id + "F46", true);
            extrude(context, id + "F47", {"entities" : qUnion([Q0]), "depth" : 127 * mm, "offsetDistance" : 25.4 * mm});
        }
        {
            var Q0;
            Q0=makeQuery(id+"F2.opExtrude","SWEPT_FACE",FACE,{"disambiguationData":[OSD([sQuery(id+"F1.wireOp",EDGE,"E24.top")])]});
            var sketch = newSketch(context, id + "F48", { "sketchPlane" : qUnion([Q0])});
            skLineSegment(sketch, "E106.bottom", {"start": v(1247.78, 889) * mm, "end": v(1228.73, 889) * mm});
            skLineSegment(sketch, "E106.top", {"start": v(1247.78, 800.1) * mm, "end": v(1228.73, 800.1) * mm});
            skLineSegment(sketch, "E106.left", {"start": v(1247.78, 889) * mm, "end": v(1247.78, 800.1) * mm});
            skLineSegment(sketch, "E106.right", {"start": v(1228.73, 889) * mm, "end": v(1228.73, 800.1) * mm});
            skSolve(sketch);
        }
        {
            var Q0;
            Q0 = qSketchRegion(id + "F48", true);
            var Q1;
            Q1=makeQuery(id+"F2.opExtrude","SWEPT_FACE",FACE,{"disambiguationData":[OSD([sQuery(id+"F1.wireOp",EDGE,"E26.top")])]});
            extrude(context, id + "F49", {"entities" : qUnion([Q0]), "endBound" : BoundingType.UP_TO_SURFACE, "depth" : 25.4 * mm, "endBoundEntityFace" : qUnion([Q1]), "offsetDistance" : 25.4 * mm});
        }
    });
